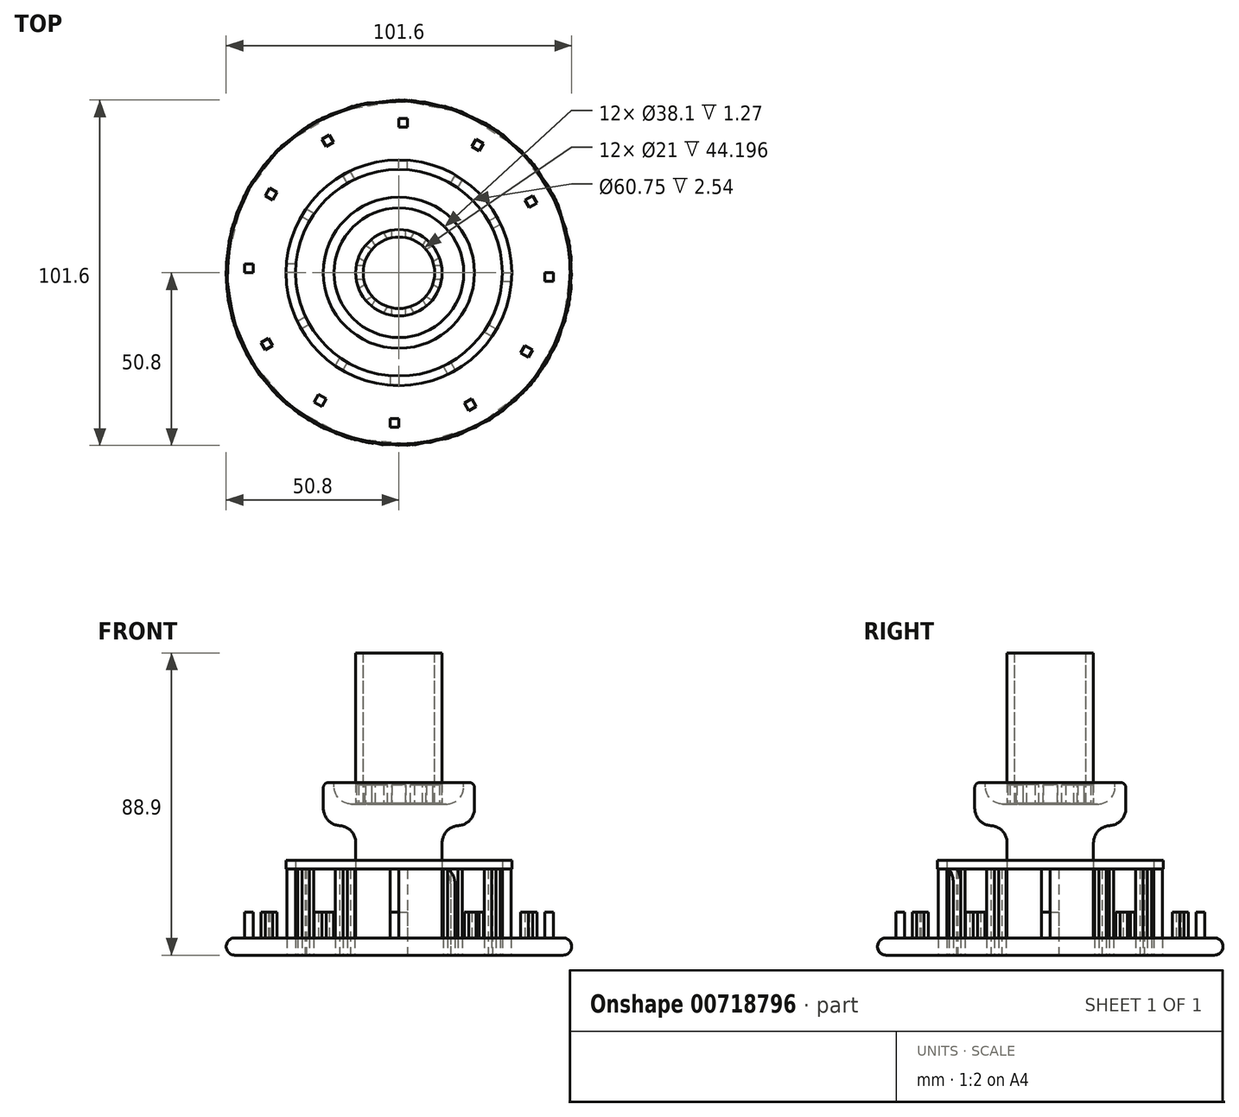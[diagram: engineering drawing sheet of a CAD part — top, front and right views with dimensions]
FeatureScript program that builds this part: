
annotation { "Feature Type Name" : "Feature", "Feature Type Description" : "" }
export const myFeature = defineFeature(function(context is Context, id is Id, definition is map)
    precondition{}
    {
        {
            var Q0;
            Q0=qCreatedBy(makeId("Top.planeOp"),FACE);
            var sketch = newSketch(context, id + "F0", { "sketchPlane" : qUnion([Q0])});
            skCircle(sketch, "E0", {"center": v(0, 0) * mm, "radius": 50.8 * mm});
            skSolve(sketch);
        }
        {
            var Q0;
            Q0=qSketchRegion(id+"F0",true);
            extrude(context, id + "F1", {"entities" : qUnion([Q0]), "depth" : 5.08 * mm, "offsetDistance" : 25.4 * mm});
        }
        {
            var Q0;
            Q0=makeQuery(id+"F1.opExtrude","SWEPT_FACE",FACE,{"disambiguationData":[OSD([sQuery(id+"F0.wireOp",EDGE,"E0")])]});
            fillet(context, id + "F2", {"entities" : qUnion([Q0]), "radius" : 2.54 * mm, "tangentPropagation" : true, "allowEdgeOverflow" : false});
        }
        {
            var Q0;
            Q0=qCreatedBy(makeId("Top.planeOp"),FACE);
            var sketch = newSketch(context, id + "F3", { "sketchPlane" : qUnion([Q0])});
            skCircle(sketch, "E1", {"center": v(0, 0) * mm, "radius": 12.7 * mm});
            skSolve(sketch);
        }
        {
            var Q0;
            Q0=qSketchRegion(id+"F3",true);
            extrude(context, id + "F4", {"entities" : qUnion([Q0]), "operationType" : NewBodyOperationType.ADD, "depth" : 88.9 * mm, "offsetDistance" : 25.4 * mm});
        }
        {
            var Q0;
            Q0=qCreatedBy(makeId("Top.planeOp"),FACE);
            var sketch = newSketch(context, id + "F5", { "sketchPlane" : qUnion([Q0])});
            skCircle(sketch, "E2", {"center": v(0, 0) * mm, "radius": 22.23 * mm});
            skSolve(sketch);
        }
        {
            var Q0;
            Q0=qSketchRegion(id+"F5",true);
            extrude(context, id + "F6", {"entities" : qUnion([Q0]), "operationType" : NewBodyOperationType.ADD, "depth" : 50.8 * mm, "offsetDistance" : 25.4 * mm, "hasSecondDirection" : true, "secondDirectionOppositeDirection" : false, "secondDirectionDepth" : 38.1 * mm});
        }
        {
            var Q0;
            Q0=makeQuery(id+"F6.opExtrude","CAP_EDGE",EDGE,{"disambiguationData":[OSD([sQuery(id+"F5.wireOp",EDGE,"E2")])],"isStart":true});
            fillet(context, id + "F7", {"entities" : qUnion([Q0]), "radius" : 5.08 * mm, "tangentPropagation" : true, "allowEdgeOverflow" : false});
        }
        {
            var Q0;
            Q0=makeQuery(id+"F6.opExtrude","CAP_FACE",FACE,{"disambiguationData":[OSD([sQuery(id+"F5.wireOp",EDGE,"E2")])],"isStart":false});
            var sketch = newSketch(context, id + "F8", { "sketchPlane" : qUnion([Q0])});
            skCircle(sketch, "E3", {"center": v(0, 0) * mm, "radius": 12.7 * mm});
            skCircle(sketch, "E4", {"center": v(0, 0) * mm, "radius": 19.05 * mm});
            skSolve(sketch);
        }
        {
            var Q0;
            Q0=qSketchRegion(id+"F8",true);
            extrude(context, id + "F9", {"entities" : qUnion([Q0]), "operationType" : NewBodyOperationType.REMOVE, "oppositeDirection" : true, "depth" : 6.35 * mm, "offsetDistance" : 25.4 * mm});
        }
        {
            var Q0;
            Q0=makeQuery(id+"F9.boolean.opBoolean","COPY",EDGE,{"derivedFrom":makeQuery(id+"F9.opExtrude","CAP_EDGE",EDGE,{"disambiguationData":[OSD([sQuery(id+"F8.wireOp",EDGE,"E4")])],"isStart":false})});
            fillet(context, id + "F10", {"entities" : qUnion([Q0]), "radius" : 5.08 * mm, "tangentPropagation" : true, "allowEdgeOverflow" : false});
        }
        {
            var Q0;
            Q0=qCreatedBy(makeId("Right.planeOp"),FACE);
            var sketch = newSketch(context, id + "F11", { "sketchPlane" : qUnion([Q0])});
            skLineSegment(sketch, "E5.right", {"start": v(-2.05, 44.7) * mm, "end": v(-2.05, 50.1) * mm});
            skLineSegment(sketch, "E6.MirrorCS", {"start": v(2.05, 44.7) * mm, "end": v(2.05, 50.1) * mm});
            skLineSegment(sketch, "E7", {"start": v(2.05, 50.1) * mm, "end": v(-2.05, 50.1) * mm});
            skLineSegment(sketch, "E8", {"start": v(2.05, 44.7) * mm, "end": v(-2.05, 44.7) * mm});
            skSolve(sketch);
        }
        {
            var Q0;
            Q0=qSketchRegion(id+"F11",true);
            extrude(context, id + "F12", {"entities" : qUnion([Q0]), "operationType" : NewBodyOperationType.REMOVE, "depth" : 12.7 * mm, "offsetDistance" : 25.4 * mm, "hasSecondDirection" : true, "secondDirectionOppositeDirection" : true, "secondDirectionDepth" : 12.7 * mm});
        }
        {
            var Q0;
            Q0=makeQuery(id+"F4.opExtrude","CAP_FACE",FACE,{"disambiguationData":[OSD([sQuery(id+"F3.wireOp",EDGE,"E1")])],"isStart":false});
            var sketch = newSketch(context, id + "F13", { "sketchPlane" : qUnion([Q0])});
            skCircle(sketch, "E9", {"center": v(0, 0) * mm, "radius": 10.5 * mm});
            skSolve(sketch);
        }
        {
            var Q0;
            Q0=qSketchRegion(id+"F13",true);
            extrude(context, id + "F14", {"entities" : qUnion([Q0]), "operationType" : NewBodyOperationType.REMOVE, "oppositeDirection" : true, "depth" : 44.2 * mm, "offsetDistance" : 25.4 * mm});
        }
        {
            var Q0;
            Q0=makeQuery(id+"F9.boolean.opBoolean","COPY",EDGE,{"derivedFrom":makeQuery(id+"F9.opExtrude","CAP_EDGE",EDGE,{"disambiguationData":[OSD([sQuery(id+"F8.wireOp",EDGE,"E4")])],"isStart":true})});
            var Q1;
            Q1=makeQuery(id+"F6.opExtrude","CAP_EDGE",EDGE,{"disambiguationData":[OSD([sQuery(id+"F5.wireOp",EDGE,"E2")])],"isStart":false});
            fillet(context, id + "F15", {"entities" : qUnion([Q0, Q1]), "radius" : 1.57 * mm, "tangentPropagation" : true, "allowEdgeOverflow" : false});
        }
        {
            var Q0;
            Q0=makeQuery(id+"F6.boolean.opBoolean","INTERSECT",EDGE,{"derivedFrom":[makeQuery(id+"F4.opExtrude","SWEPT_FACE",FACE,{"disambiguationData":[OSD([sQuery(id+"F3.wireOp",EDGE,"E1")])]}),makeQuery(id+"F6.opExtrude","CAP_FACE",FACE,{"disambiguationData":[OSD([sQuery(id+"F5.wireOp",EDGE,"E2")])],"isStart":true})]});
            fillet(context, id + "F16", {"entities" : qUnion([Q0]), "radius" : 5.08 * mm, "tangentPropagation" : true, "allowEdgeOverflow" : false});
        }
        {
            var Q0;
            Q0=qCreatedBy(makeId("Front.planeOp"),FACE);
            var sketch = newSketch(context, id + "F17", { "sketchPlane" : qUnion([Q0])});
            skLineSegment(sketch, "E10", {"start": v(0, 0) * mm, "end": v(0, 97) * mm, "construction": true});
            skSolve(sketch);
        }
        {
            var Q0;
            Q0=qCreatedBy(makeId("Top.planeOp"),FACE);
            var sketch = newSketch(context, id + "F18", { "sketchPlane" : qUnion([Q0])});
            skLineSegment(sketch, "E11.bottom", {"start": v(30.38, 0) * mm, "end": v(32.92, 0) * mm});
            skLineSegment(sketch, "E11.top", {"start": v(30.38, -2.54) * mm, "end": v(32.92, -2.54) * mm});
            skLineSegment(sketch, "E11.left", {"start": v(30.38, 0) * mm, "end": v(30.38, -2.54) * mm});
            skLineSegment(sketch, "E11.right", {"start": v(32.92, 0) * mm, "end": v(32.92, -2.54) * mm});
            skSolve(sketch);
        }
        {
            var Q0;
            Q0=qSketchRegion(id+"F18",true);
            extrude(context, id + "F19", {"entities" : qUnion([Q0]), "depth" : 25.4 * mm, "offsetDistance" : 25.4 * mm});
        }
        {
            var Q0;
            Q0=qCreatedBy(makeId("Top.planeOp"),FACE);
            var sketch = newSketch(context, id + "F20", { "sketchPlane" : qUnion([Q0])});
            skLineSegment(sketch, "E12.bottom", {"start": v(42.84, 0) * mm, "end": v(45.38, 0) * mm});
            skLineSegment(sketch, "E12.top", {"start": v(42.84, -2.54) * mm, "end": v(45.38, -2.54) * mm});
            skLineSegment(sketch, "E12.left", {"start": v(42.84, 0) * mm, "end": v(42.84, -2.54) * mm});
            skLineSegment(sketch, "E12.right", {"start": v(45.38, 0) * mm, "end": v(45.38, -2.54) * mm});
            skSolve(sketch);
        }
        {
            var Q0;
            Q0=qSketchRegion(id+"F20",true);
            extrude(context, id + "F21", {"entities" : qUnion([Q0]), "operationType" : NewBodyOperationType.ADD, "depth" : 12.7 * mm, "offsetDistance" : 25.4 * mm});
        }
        {
            var Q0;
            Q0=makeQuery(id+"F1.opExtrude","SWEPT_BODY",BODY,{"disambiguationData":[OSD([sQuery(id+"F0.wireOp",EDGE,"E0")])]});
            var Q1;
            Q1=makeQuery(id+"F19.opExtrude","SWEPT_BODY",BODY,{"disambiguationData":[OSD([sQuery(id+"F18.wireOp",EDGE,"E11.bottom"),sQuery(id+"F18.wireOp",EDGE,"E11.top"),sQuery(id+"F18.wireOp",EDGE,"E11.left"),sQuery(id+"F18.wireOp",EDGE,"E11.right")])]});
            var Q2;
            Q2=sQuery(id+"F17.wireOp",EDGE,"E10");
            circularPattern(context, id + "F22", {"entities" : qUnion([Q0, Q1]), "axis" : qUnion([Q2]), "angle" : 360 * degree, "instanceCount" : 12, "equalSpace" : true});
        }
        {
            var Q0;
            Q0=qCreatedBy(makeId("Top.planeOp"),FACE);
            var sketch = newSketch(context, id + "F23", { "sketchPlane" : qUnion([Q0])});
            skCircle(sketch, "E13", {"center": v(0, 0) * mm, "radius": 30.38 * mm});
            skCircle(sketch, "E14", {"center": v(0, 0) * mm, "radius": 33.2 * mm});
            skSolve(sketch);
        }
        {
            var Q0;
            Q0=qSketchRegion(id+"F23",true);
            extrude(context, id + "F24", {"entities" : qUnion([Q0]), "depth" : 27.94 * mm, "offsetDistance" : 25.4 * mm, "hasSecondDirection" : true, "secondDirectionOppositeDirection" : false, "secondDirectionDepth" : 25.4 * mm});
        }
        {
            var Q0;
            Q0=makeQuery(id+"F22.opPattern","COPY",EDGE,{"derivedFrom":makeQuery(id+"F19.opExtrude","CAP_EDGE",EDGE,{"disambiguationData":[OSD([sQuery(id+"F18.wireOp",EDGE,"E11.bottom")])],"isStart":false}),"instanceName":"10"});
            fillet(context, id + "F25", {"entities" : qUnion([Q0]), "radius" : 5.08 * mm, "tangentPropagation" : true, "allowEdgeOverflow" : false});
        }
    });
